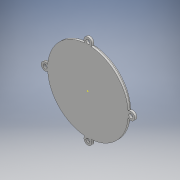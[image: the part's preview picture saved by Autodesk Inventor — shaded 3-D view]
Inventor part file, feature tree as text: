
AUTODESK INVENTOR PART (.ipt)
format: ipt  version: 2018 (Build 220112000, 112)  size: 156,160 bytes
history: native  units: mm
features: sketch x4, extrude x3, projected_geometry x1
ambient origin geometry x8: Origin, YZ Plane, XZ Plane, XY Plane, X Axis, Y Axis, Z Axis, Center Point
bodies: Solid1 (feature_tree)
feature tree (8):
  extrude  "Extrusion1"  Depth=1.0mm TaperAngle=0.0deg
  extrude  "Extrusion2"  Depth=2.0mm
  sketch  "Sketch3"  dims[d6=1.0mm d7=0.0mm]
  extrude  "Extrusion3"  [1 undecoded]
  sketch  "Sketch1"  dims[d0=19.0mm d1=1.0mm d2=0.0mm]
  sketch  "Sketch2"  dims[d3=2.0mm d4=0.0mm d5=36.0mm]
  projected_geometry  "Projected Loop1"
  sketch  "Sketch4"
note: 1 required parameter value undecoded (feature->parameter linkage not recoverable at this tier; creation-order binding heuristic only, values carry confidence <= 0.55)
